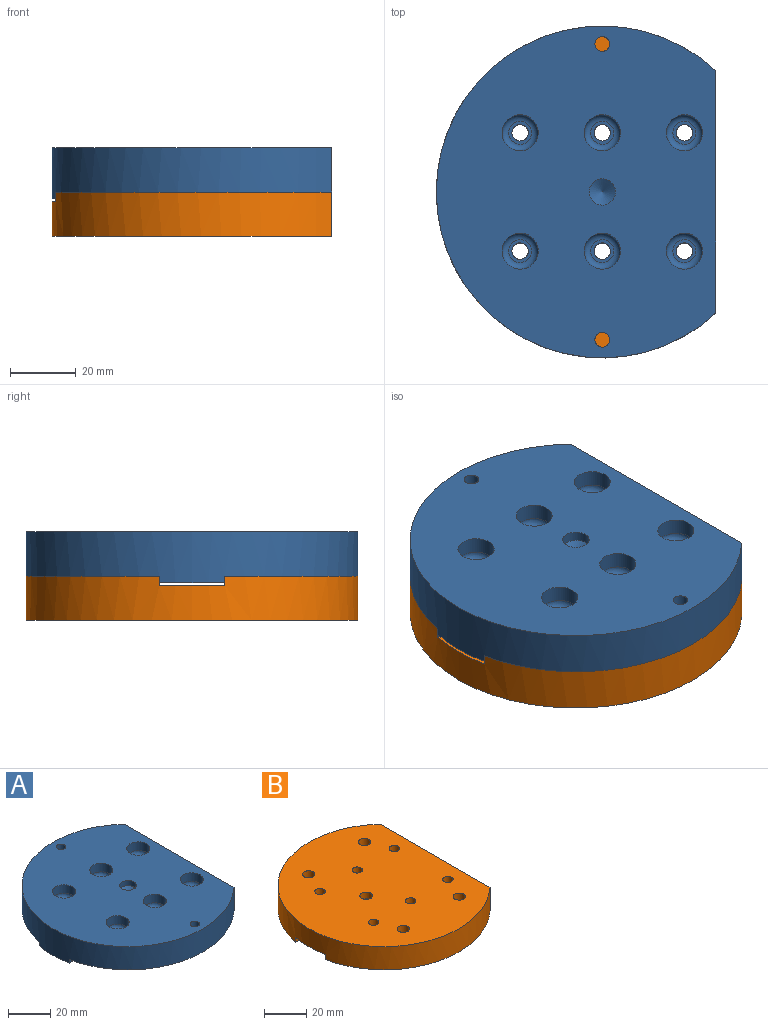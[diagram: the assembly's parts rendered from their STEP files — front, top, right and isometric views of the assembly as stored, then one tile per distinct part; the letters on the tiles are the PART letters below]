
ASSEMBLY  parts=2 mates=1
PART A: 38 faces, bbox 85x101x15.6 mm
  f0: plane 84x40.5mm, normal (0,0,-1), area 2676.6mm2, adj f2,f4,f5,f8,f11,f29,f34
  f1: plane 84x40.5mm, normal (0,0,-1), area 2676.6mm2, adj f2,f4,f17,f20,f23,f30,f35
  f2: cylinder r=50.5mm len=101mm, axis (0,0,-1), area 3208.5mm2, adj f0,f1,f3,f4,f29,f30,f31
  f3: plane 101x85mm, normal (0,0,1), area 6544mm2, adj f2,f4,f7,f10,f13,f19,f22,f25
  f4: plane 73.76x15.55mm, normal (1,0,0), area 1036.7mm2, adj f0,f1,f2,f3,f29,f30,f31
  f5: cylinder r=2.5mm len=6.5mm, axis (0,0,1), area 102.1mm2, adj f0,f6
  f6: plane 7x7mm, normal (0,0,1), area 18.8mm2, adj f5,f14
  f7: cylinder r=5.5mm len=11mm, axis (0,0,1), area 172.8mm2, adj f3,f14
  f8: cylinder r=2.5mm len=6.5mm, axis (0,0,1), area 102.1mm2, adj f0,f9
  f9: plane 7x7mm, normal (0,0,1), area 18.8mm2, adj f8,f15
  f10: cylinder r=5.5mm len=11mm, axis (0,0,1), area 172.8mm2, adj f3,f15
  f11: cylinder r=2.5mm len=6.5mm, axis (0,0,1), area 102.1mm2, adj f0,f12
  f12: plane 7x7mm, normal (0,0,1), area 18.8mm2, adj f11,f16
  f13: cylinder r=5.5mm len=11mm, axis (0,0,1), area 172.8mm2, adj f3,f16
  f14: torus R=3.5mm, axis (0,0,1), area 94.2mm2, adj f6,f7
  f15: torus R=3.5mm, axis (0,0,1), area 94.2mm2, adj f9,f10
  f16: torus R=3.5mm, axis (0,0,1), area 94.2mm2, adj f12,f13
  f17: cylinder r=2.5mm len=6.5mm, axis (0,0,1), area 102.1mm2, adj f1,f18
  f18: plane 7x7mm, normal (0,0,1), area 18.8mm2, adj f17,f26
  f19: cylinder r=5.5mm len=11mm, axis (0,0,1), area 172.8mm2, adj f3,f26
  f20: cylinder r=2.5mm len=6.5mm, axis (0,0,1), area 102.1mm2, adj f1,f21
  f21: plane 7x7mm, normal (0,0,1), area 18.8mm2, adj f20,f27
  f22: cylinder r=5.5mm len=11mm, axis (0,0,1), area 172.8mm2, adj f3,f27
  f23: cylinder r=2.5mm len=6.5mm, axis (0,0,1), area 102.1mm2, adj f1,f24
  f24: plane 7x7mm, normal (0,0,1), area 18.8mm2, adj f23,f28
  f25: cylinder r=5.5mm len=11mm, axis (0,0,1), area 172.8mm2, adj f3,f28
  f26: torus R=3.5mm, axis (0,0,1), area 94.2mm2, adj f18,f19
  f27: torus R=3.5mm, axis (0,0,1), area 94.2mm2, adj f21,f22
  f28: torus R=3.5mm, axis (0,0,1), area 94.2mm2, adj f24,f25
  f29: plane 84x2.05mm, normal (0,-1,0), area 172.2mm2, adj f0,f2,f4,f31
  f30: plane 84x2.05mm, normal (0,1,0), area 172.2mm2, adj f1,f2,f4,f31
  f31: plane 85x20mm, normal (0,0,-1), area 1665.1mm2, adj f2,f4,f29,f30,f33
  f32: cone r=0mm half-angle=59deg, axis (0,0,-1), area 33mm2, adj f33
  f33: cylinder r=3mm len=7mm, axis (0,0,-1), area 131.9mm2, adj f31,f32
  f34: cylinder r=2.25mm len=13.5mm, axis (0,0,-1), area 190.9mm2, adj f0,f3
  f35: cylinder r=2.25mm len=13.5mm, axis (0,0,-1), area 190.9mm2, adj f1,f3
  f36: cone r=0mm half-angle=59deg, axis (0,0,1), area 58.6mm2, adj f37
  f37: cylinder r=4mm len=8mm, axis (0,0,1), area 75.4mm2, adj f3,f36
PART B: 29 faces, bbox 85x101x13.5 mm
  f0: cylinder r=2.5mm len=5.2mm, axis (0,0,-1), area 81.7mm2, adj f8,f22
  f1: plane 84x40.5mm, normal (0,0,-1), area 2547.8mm2, adj f3,f5,f6,f10,f13,f23,f24,f25
  f2: plane 84x40.5mm, normal (0,0,-1), area 2547.8mm2, adj f3,f5,f7,f16,f19,f26,f27,f28
  f3: cylinder r=50.5mm len=101mm, axis (0,0,-1), area 3106.9mm2, adj f1,f2,f4,f5,f6,f7,f8
  f4: plane 101x85mm, normal (0,0,1), area 6942.3mm2, adj f3,f5,f9,f12,f15,f18,f21,f23
  f5: plane 73.76x13.5mm, normal (1,0,0), area 935.7mm2, adj f1,f2,f3,f4,f6,f7,f8
  f6: plane 84x3mm, normal (0,1,0), area 252mm2, adj f1,f3,f5,f8
  f7: plane 84x3mm, normal (0,-1,0), area 252mm2, adj f2,f3,f5,f8
  f8: plane 85x20mm, normal (0,0,-1), area 1673.7mm2, adj f0,f3,f5,f6,f7
  f9: cylinder r=2.93mm len=6.7mm, axis (0,0,-1), area 123.3mm2, adj f4,f11
  f10: cylinder r=4.8mm len=9.6mm, axis (0,0,-1), area 144.9mm2, adj f1,f11
  f11: torus R=2.8mm, axis (0,0,1), area 78.1mm2, adj f9,f10
  f12: cylinder r=2.93mm len=6.7mm, axis (0,0,-1), area 123.3mm2, adj f4,f14
  f13: cylinder r=4.8mm len=9.6mm, axis (0,0,-1), area 144.9mm2, adj f1,f14
  f14: torus R=2.8mm, axis (0,0,1), area 78.1mm2, adj f12,f13
  f15: cylinder r=2.93mm len=6.7mm, axis (0,0,-1), area 123.3mm2, adj f4,f17
  f16: cylinder r=4.8mm len=9.6mm, axis (0,0,-1), area 144.9mm2, adj f2,f17
  f17: torus R=2.8mm, axis (0,0,1), area 78.1mm2, adj f15,f16
  f18: cylinder r=2.93mm len=6.7mm, axis (0,0,-1), area 123.3mm2, adj f4,f20
  f19: cylinder r=4.8mm len=9.6mm, axis (0,0,-1), area 144.9mm2, adj f2,f20
  f20: torus R=2.8mm, axis (0,0,1), area 78.1mm2, adj f18,f19
  f21: cylinder r=3mm len=6mm, axis (0,0,1), area 75mm2, adj f4,f22
  f22: torus R=1mm, axis (0,0,-1), area 25.7mm2, adj f0,f21
  f23: cylinder r=2.5mm len=13.5mm, axis (0,0,-1), area 212.1mm2, adj f1,f4
  f24: cylinder r=2.5mm len=13.5mm, axis (0,0,-1), area 212.1mm2, adj f1,f4
  f25: cylinder r=2.5mm len=13.5mm, axis (0,0,-1), area 212.1mm2, adj f1,f4
  f26: cylinder r=2.5mm len=13.5mm, axis (0,0,-1), area 212.1mm2, adj f2,f4
  f27: cylinder r=2.5mm len=13.5mm, axis (0,0,-1), area 212.1mm2, adj f2,f4
  f28: cylinder r=2.5mm len=13.5mm, axis (0,0,-1), area 212.1mm2, adj f2,f4
PLACE A t=(26.78,0.74,13.09)mm
PLACE B rot(axis=(1,0,0),180deg) t=(26.78,0.74,13.09)mm
MATE fastened B.f24 <-> A.f20  axis (0,0,1) through (26.78,18.74,13.09)mm
